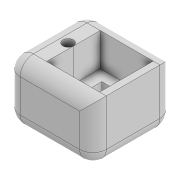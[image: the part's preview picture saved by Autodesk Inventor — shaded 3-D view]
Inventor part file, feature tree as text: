
AUTODESK INVENTOR PART (.ipt)
format: ipt  version: 2022 (Build 260153000, 153)  size: 158,720 bytes
history: native  units: mm
features: extrude x4, sketch x4, fillet x1, projected_geometry x1
ambient origin geometry x8: Origin, YZ Plane, XZ Plane, XY Plane, X Axis, Y Axis, Z Axis, Center Point
bodies: Solid1 (feature_tree)
feature tree (10):
  extrude  "Extrusion1"  Depth=8.0mm
  extrude  "Extrusion2"  Depth=2.0mm
  extrude  "Extrusion3"  Depth=4.0mm
  extrude  "Extrusion4"  Depth=4.0mm TaperAngle=0.0deg
  fillet  "Fillet1"  Radius=1.6mm
  sketch  "Sketch1"  dims[d0=8.1mm d1=8.0mm]
  sketch  "Sketch2"  dims[d5=2.0mm d6=2.0mm]
  projected_geometry  "Projected Loop1"
  sketch  "Sketch3"  dims[d7=1.0mm d8=4.0mm]
  sketch  "Sketch4"  dims[d9=5.0mm d10=0.0mm d11=4.0mm d12=0.0mm d14=1.6mm d15=100.0mm d16=0.0mm d17=5.0mm d18=3.8mm d19=2.0mm d20=100.0mm d21=0.0mm d22=2.0mm]
